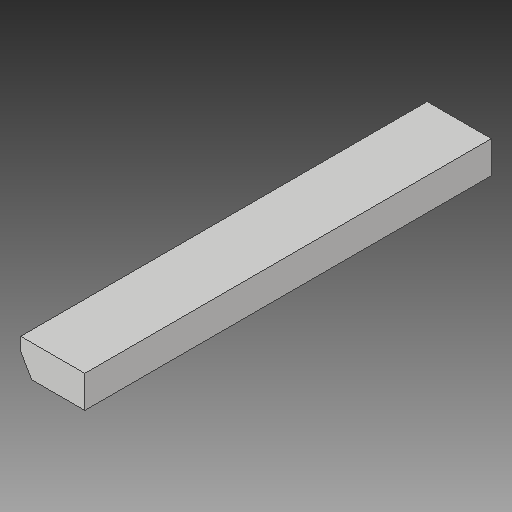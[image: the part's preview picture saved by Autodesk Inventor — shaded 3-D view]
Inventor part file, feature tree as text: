
AUTODESK INVENTOR PART (.ipt)
format: ipt  version: 2017 (Build 210142000, 142)  size: 100,352 bytes
history: native  units: in
note: dims shown in document units (in); Inventor stores cm internally (conversion verified against a paired STEP export)
features: other x3, extrude x2, sketch x2, reference x1
ambient origin geometry x8: Origin, YZ Plane, XZ Plane, XY Plane, X Axis, Y Axis, Z Axis, Center Point
bodies: Solid1 (feature_tree)
feature tree (8):
  extrude  "Extrusion1"  Depth=9.5in
  extrude  "Extrusion2"  TaperAngle=120.0deg  [1 undecoded]
  sketch  "Sketch1"  dims[d0=1.5in d1=9.5in]
  sketch  "Sketch2"  dims[d2=0.75in d3=0.0in d4=120.0deg d5=9.5in d6=0.0in]
  reference  "Reference1"
  parser-record x1  (decoder bookkeeping rows leaked as tree rows — omitted from the tree; the rows remain in map.json)
  other  "Arcade.iam"
  other  "screen_holder:1"
note: 1 required parameter value undecoded (feature->parameter linkage not recoverable at this tier; creation-order binding heuristic only, values carry confidence <= 0.55)
note: 1 file-system path scrubbed to <path> (originals preserved in map.json)
